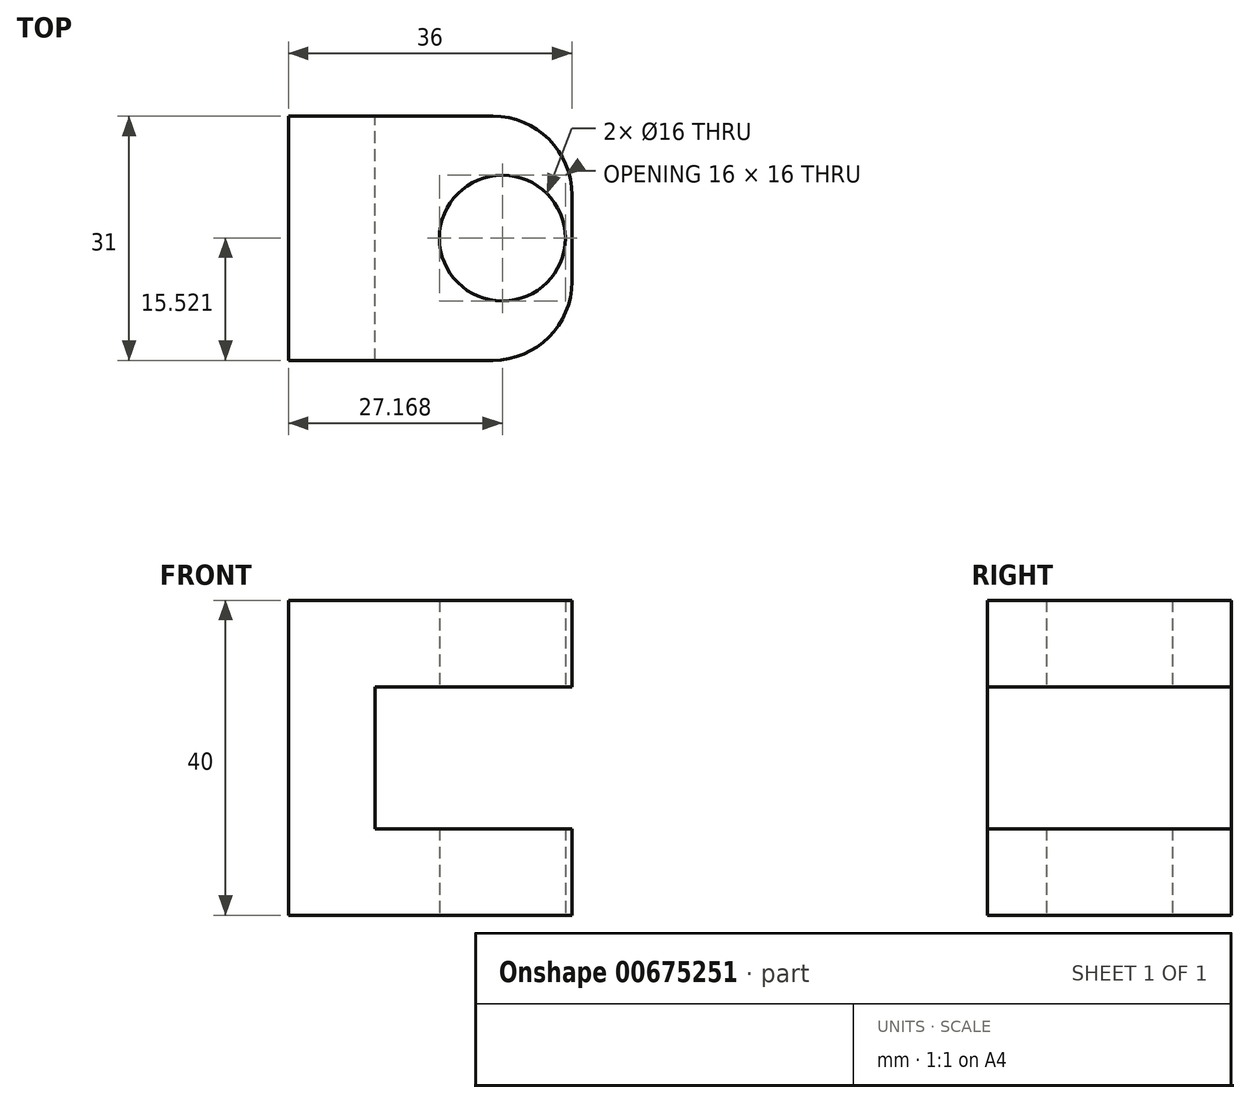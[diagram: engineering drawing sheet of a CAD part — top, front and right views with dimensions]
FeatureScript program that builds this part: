
annotation { "Feature Type Name" : "Feature", "Feature Type Description" : "" }
export const myFeature = defineFeature(function(context is Context, id is Id, definition is map)
    precondition{}
    {
        {
            var Q0;
            Q0=qCreatedBy(makeId("Front.planeOp"),FACE);
            var sketch = newSketch(context, id + "F0", { "sketchPlane" : qUnion([Q0])});
            skLineSegment(sketch, "E0", {"start": v(18, 40) * mm, "end": v(-18, 40) * mm});
            skLineSegment(sketch, "E1", {"start": v(-18, 40) * mm, "end": v(-18, 0) * mm});
            skLineSegment(sketch, "E2", {"start": v(-18, 0) * mm, "end": v(18, 0) * mm});
            skLineSegment(sketch, "E3", {"start": v(-7, 40) * mm, "end": v(-7, 0) * mm});
            skLineSegment(sketch, "E4", {"start": v(-18, 11) * mm, "end": v(18, 11) * mm});
            skLineSegment(sketch, "E5", {"start": v(-18, 29) * mm, "end": v(18, 29) * mm});
            skLineSegment(sketch, "E6", {"start": v(18, 29) * mm, "end": v(18, 40) * mm});
            skLineSegment(sketch, "E7", {"start": v(18, 11) * mm, "end": v(18, 0) * mm});
            skSolve(sketch);
        }
        {
            var Q0;
            Q0 = qSketchRegion(id + "F0", true);
            extrude(context, id + "F1", {"entities" : qUnion([Q0]), "depth" : 31 * mm, "offsetDistance" : 25 * mm});
        }
        {
            var Q0;
            Q0=qCreatedBy(makeId("Top.planeOp"),FACE);
            var sketch = newSketch(context, id + "F2", { "sketchPlane" : qUnion([Q0])});
            skPoint(sketch, "E8", {"position": v(9.17, -15.48) * mm});
            skSolve(sketch);
        }
        {
            var Q0;
            Q0=sQuery(id+"F2.wireOp",VERTEX,"E8");
            var Q1;
            Q1=makeQuery(id+"F1.opExtrude","SWEPT_BODY",BODY,{"disambiguationData":[OSD([sQuery(id+"F0.wireOp",EDGE,"E0"),sQuery(id+"F0.wireOp",EDGE,"E1"),sQuery(id+"F0.wireOp",EDGE,"E2"),sQuery(id+"F0.wireOp",EDGE,"E3"),sQuery(id+"F0.wireOp",EDGE,"E4"),sQuery(id+"F0.wireOp",EDGE,"E5"),sQuery(id+"F0.wireOp",EDGE,"E6"),sQuery(id+"F0.wireOp",EDGE,"E7")])]});
            hole(context, id + "F3", {"style" : HoleStyle.SIMPLE, "endStyle" : HoleEndStyle.THROUGH, "oppositeDirection" : true, "holeDiameter" : 16 * mm, "majorDiameter" : 5 * mm, "isTappedThrough" : true, "tappedDepth" : 12 * mm, "tapClearance" : 3, "locations" : qUnion([Q0]), "scope" : qUnion([Q1])});
        }
        {
            var Q0;
            Q0=makeQuery(id+"F1.opExtrude","CAP_EDGE",EDGE,{"disambiguationData":[OSD([sQuery(id+"F0.wireOp",EDGE,"E7")])],"isStart":true});
            var Q1;
            Q1=makeQuery(id+"F1.opExtrude","CAP_EDGE",EDGE,{"disambiguationData":[OSD([sQuery(id+"F0.wireOp",EDGE,"E6")])],"isStart":true});
            var Q2;
            Q2=makeQuery(id+"F1.opExtrude","CAP_EDGE",EDGE,{"disambiguationData":[OSD([sQuery(id+"F0.wireOp",EDGE,"E7")])],"isStart":false});
            var Q3;
            Q3=makeQuery(id+"F1.opExtrude","CAP_EDGE",EDGE,{"disambiguationData":[OSD([sQuery(id+"F0.wireOp",EDGE,"E6")])],"isStart":false});
            fillet(context, id + "F4", {"entities" : qUnion([Q0, Q1, Q2, Q3]), "radius" : 10 * mm, "tangentPropagation" : true, "allowEdgeOverflow" : false});
        }
    });
